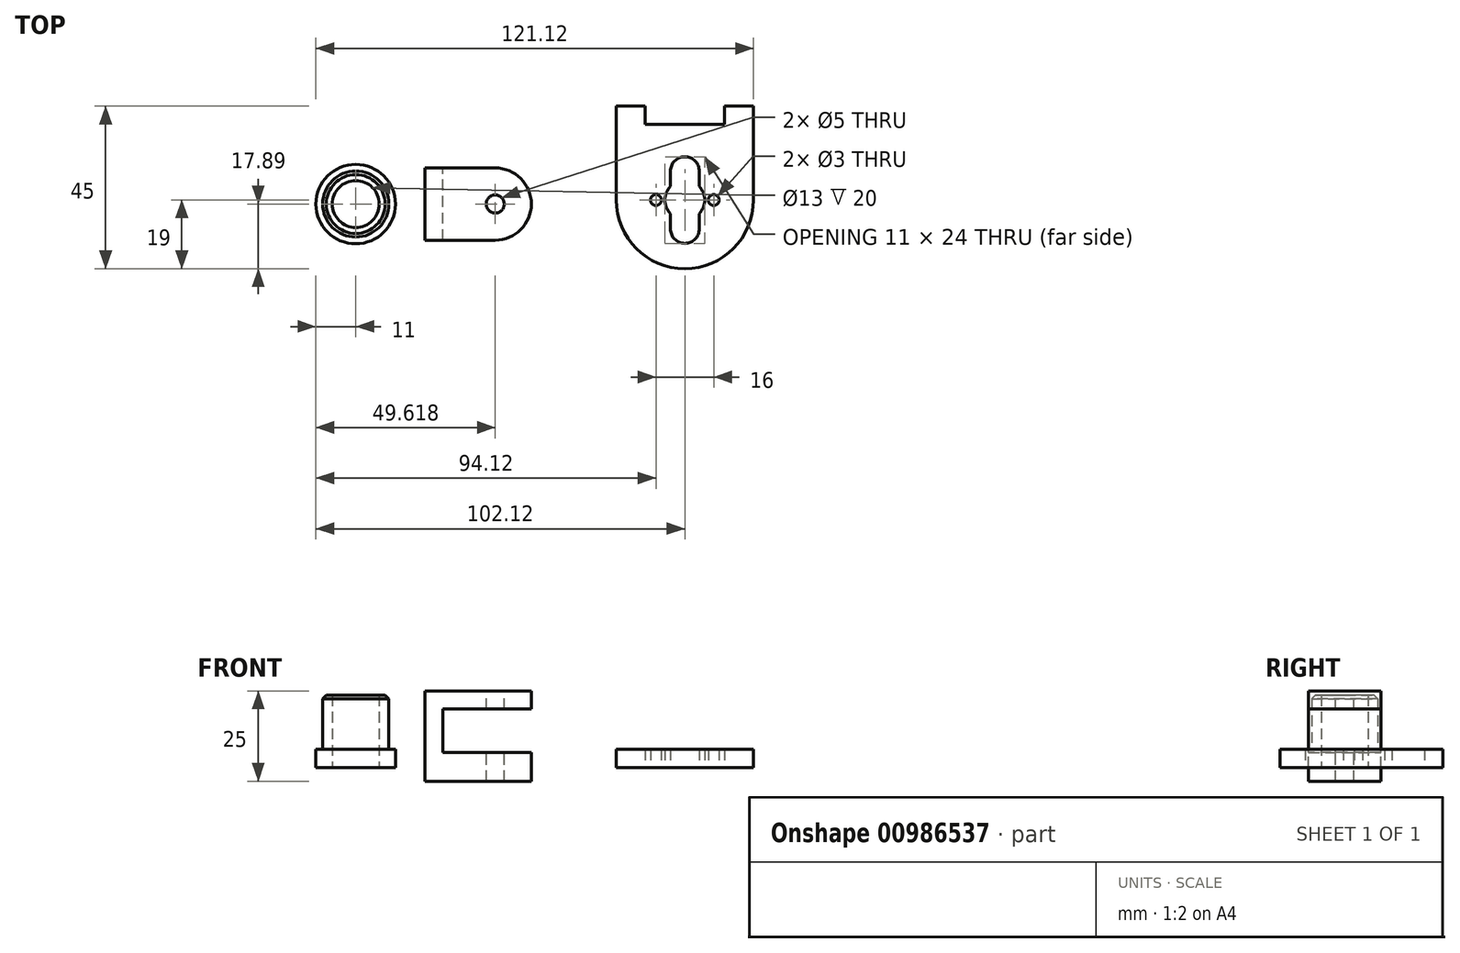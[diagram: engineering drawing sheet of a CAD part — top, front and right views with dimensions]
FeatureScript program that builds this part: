
annotation { "Feature Type Name" : "Feature", "Feature Type Description" : "" }
export const myFeature = defineFeature(function(context is Context, id is Id, definition is map)
    precondition{}
    {
        {
            var Q0;
            Q0=qCreatedBy(makeId("Top.planeOp"),FACE);
            var sketch = newSketch(context, id + "F0", { "sketchPlane" : qUnion([Q0])});
            skCircle(sketch, "E0", {"center": v(0, 0) * mm, "radius": 9.15 * mm});
            skCircle(sketch, "E1", {"center": v(0, 0) * mm, "radius": 6.5 * mm});
            skCircle(sketch, "E2", {"center": v(0, 0) * mm, "radius": 11 * mm});
            skSolve(sketch);
        }
        {
            var Q0;
            Q0=makeQuery(id+"F0.imprint","IMPRINT",FACE,{"disambiguationData":[TD([[makeQuery(id+"F0.imprint","IMPRINT",EDGE,{"derivedFrom":sQuery(id+"F0.wireOp",EDGE,"E0")}),1.0]])]});
            extrude(context, id + "F1", {"entities" : qUnion([Q0]), "depth" : 20 * mm, "offsetDistance" : 25 * mm});
        }
        {
            var Q0;
            Q0=makeQuery(id+"F0.imprint","IMPRINT",FACE,{"disambiguationData":[TD([[makeQuery(id+"F0.imprint","IMPRINT",EDGE,{"derivedFrom":sQuery(id+"F0.wireOp",EDGE,"E0")}),-1.0]])]});
            extrude(context, id + "F2", {"entities" : qUnion([Q0]), "operationType" : NewBodyOperationType.ADD, "depth" : 5 * mm, "offsetDistance" : 25 * mm});
        }
        {
            var Q0;
            Q0=makeQuery(id+"F1.opExtrude","CAP_EDGE",EDGE,{"disambiguationData":[OSD([sQuery(id+"F0.wireOp",EDGE,"E0")])],"isStart":false});
            chamfer(context, id + "F3", {"entities" : qUnion([Q0]), "width" : 1 * mm, "tangentPropagation" : true});
        }
        {
            var Q0;
            Q0=qCreatedBy(makeId("Front.planeOp"),FACE);
            var sketch = newSketch(context, id + "F4", { "sketchPlane" : qUnion([Q0])});
            skLineSegment(sketch, "E3", {"start": v(48.62, 21.18) * mm, "end": v(19.12, 21.18) * mm});
            skLineSegment(sketch, "E4", {"start": v(19.12, 21.18) * mm, "end": v(19.12, -3.82) * mm});
            skLineSegment(sketch, "E5", {"start": v(19.12, -3.82) * mm, "end": v(48.62, -3.82) * mm});
            skLineSegment(sketch, "E6", {"start": v(48.62, -3.82) * mm, "end": v(48.62, 4.18) * mm});
            skLineSegment(sketch, "E7", {"start": v(48.62, 4.18) * mm, "end": v(24.12, 4.18) * mm});
            skLineSegment(sketch, "E8", {"start": v(24.12, 4.18) * mm, "end": v(24.12, 16.18) * mm});
            skLineSegment(sketch, "E9", {"start": v(24.12, 16.18) * mm, "end": v(48.62, 16.18) * mm});
            skLineSegment(sketch, "E10", {"start": v(48.62, 16.18) * mm, "end": v(48.62, 21.18) * mm});
            skLineSegment(sketch, "E11", {"start": v(38.62, 21.18) * mm, "end": v(38.62, -3.82) * mm, "construction": true});
            skSolve(sketch);
        }
        {
            var Q0;
            Q0=makeQuery(id+"F4.imprint","IMPRINT",FACE,{"disambiguationData":[TD([[makeQuery(id+"F4.imprint","IMPRINT",EDGE,{"derivedFrom":sQuery(id+"F4.wireOp",EDGE,"E3")}),1.0]])]});
            extrude(context, id + "F5", {"entities" : qUnion([Q0]), "endBound" : BoundingType.SYMMETRIC, "depth" : 20 * mm, "offsetDistance" : 25 * mm});
        }
        {
            var Q0;
            Q0=makeQuery(id+"F5.opExtrude","CAP_EDGE",EDGE,{"disambiguationData":[OSD([sQuery(id+"F4.wireOp",EDGE,"E10")])],"isStart":false});
            var Q1;
            Q1=makeQuery(id+"F5.opExtrude","CAP_EDGE",EDGE,{"disambiguationData":[OSD([sQuery(id+"F4.wireOp",EDGE,"E10")])],"isStart":true});
            var Q2;
            Q2=makeQuery(id+"F5.opExtrude","CAP_EDGE",EDGE,{"disambiguationData":[OSD([sQuery(id+"F4.wireOp",EDGE,"E6")])],"isStart":true});
            var Q3;
            Q3=makeQuery(id+"F5.opExtrude","CAP_EDGE",EDGE,{"disambiguationData":[OSD([sQuery(id+"F4.wireOp",EDGE,"E6")])],"isStart":false});
            fillet(context, id + "F6", {"entities" : qUnion([Q0, Q1, Q2, Q3]), "radius" : 10 * mm, "tangentPropagation" : true, "allowEdgeOverflow" : false});
        }
        {
            var Q0;
            Q0=makeQuery(id+"F5.opExtrude","SWEPT_FACE",FACE,{"disambiguationData":[OSD([sQuery(id+"F4.wireOp",EDGE,"E3")])]});
            var sketch = newSketch(context, id + "F7", { "sketchPlane" : qUnion([Q0])});
            skPoint(sketch, "E12.0", {"position": v(38.62, 0) * mm});
            skCircle(sketch, "E13", {"center": v(38.62, 0) * mm, "radius": 2.5 * mm});
            skSolve(sketch);
        }
        {
            var Q0;
            Q0=makeQuery(id+"F7.imprint","IMPRINT",FACE,{"disambiguationData":[TD([[makeQuery(id+"F7.imprint","IMPRINT",EDGE,{"derivedFrom":sQuery(id+"F7.wireOp",EDGE,"E13")}),1.0]])]});
            extrude(context, id + "F8", {"entities" : qUnion([Q0]), "operationType" : NewBodyOperationType.REMOVE, "endBound" : BoundingType.THROUGH_ALL, "oppositeDirection" : true, "depth" : 25 * mm, "offsetDistance" : 25 * mm});
        }
        {
            var Q0;
            Q0=qCreatedBy(makeId("Top.planeOp"),FACE);
            var sketch = newSketch(context, id + "F9", { "sketchPlane" : qUnion([Q0])});
            skArc(sketch, "E14", {"start": v(72.12, 1.1) * mm, "mid": v(91.12, -17.9) * mm, "end": v(110.12, 1.1) * mm});
            skLineSegment(sketch, "E15", {"start": v(72.12, 1.1) * mm, "end": v(72.12, 27.1) * mm});
            skLineSegment(sketch, "E16", {"start": v(72.12, 27.1) * mm, "end": v(80.12, 27.1) * mm});
            skLineSegment(sketch, "E17", {"start": v(80.12, 27.1) * mm, "end": v(80.12, 22.1) * mm});
            skLineSegment(sketch, "E18", {"start": v(80.12, 22.1) * mm, "end": v(102.12, 22.1) * mm});
            skLineSegment(sketch, "E19", {"start": v(102.12, 22.1) * mm, "end": v(102.12, 27.1) * mm});
            skLineSegment(sketch, "E20", {"start": v(102.12, 27.1) * mm, "end": v(110.12, 27.1) * mm});
            skLineSegment(sketch, "E21", {"start": v(110.12, 27.1) * mm, "end": v(110.12, 1.1) * mm});
            skLineSegment(sketch, "E22", {"start": v(91.12, 1.1) * mm, "end": v(91.12, 27.1) * mm, "construction": true});
            skCircle(sketch, "E23", {"center": v(83.12, 1.1) * mm, "radius": 1.5 * mm});
            skCircle(sketch, "E24", {"center": v(99.12, 1.1) * mm, "radius": 1.5 * mm});
            skCircle(sketch, "E25", {"center": v(91.12, 1.1) * mm, "radius": 11 * mm, "construction": true});
            skArc(sketch, "E26", {"start": v(87.12, 4.88) * mm, "mid": v(85.62, 1.1) * mm, "end": v(87.12, -2.67) * mm});
            skCircle(sketch, "E27", {"center": v(91.12, 9.1) * mm, "radius": 1.5 * mm, "construction": true});
            skCircle(sketch, "E28", {"center": v(91.12, -6.9) * mm, "radius": 1.5 * mm, "construction": true});
            skArc(sketch, "E29", {"start": v(95.12, 9.1) * mm, "mid": v(91.12, 13.1) * mm, "end": v(87.12, 9.1) * mm});
            skLineSegment(sketch, "E30", {"start": v(87.12, 9.1) * mm, "end": v(87.12, 4.88) * mm});
            skArc(sketch, "E31", {"start": v(87.12, -6.9) * mm, "mid": v(91.12, -10.9) * mm, "end": v(95.12, -6.9) * mm});
            skLineSegment(sketch, "E32", {"start": v(95.12, -6.9) * mm, "end": v(95.12, -2.67) * mm});
            skLineSegment(sketch, "E33.trimOffspring", {"start": v(87.12, -2.67) * mm, "end": v(87.12, -6.9) * mm});
            skLineSegment(sketch, "E34.trimOffspring", {"start": v(95.12, 4.88) * mm, "end": v(95.12, 9.1) * mm});
            skLineSegment(sketch, "E35", {"start": v(110.12, 1.1) * mm, "end": v(72.12, 1.1) * mm, "construction": true});
            skArc(sketch, "E36.trimOffspring", {"start": v(95.12, -2.67) * mm, "mid": v(96.62, 1.1) * mm, "end": v(95.12, 4.88) * mm});
            skSolve(sketch);
        }
        {
            var Q0;
            Q0=makeQuery(id+"F9.imprint","IMPRINT",FACE,{"disambiguationData":[TD([[makeQuery(id+"F9.imprint","IMPRINT",EDGE,{"derivedFrom":sQuery(id+"F9.wireOp",EDGE,"E14")}),1.0]])]});
            extrude(context, id + "F10", {"entities" : qUnion([Q0]), "depth" : 5 * mm, "offsetDistance" : 25 * mm});
        }
    });
